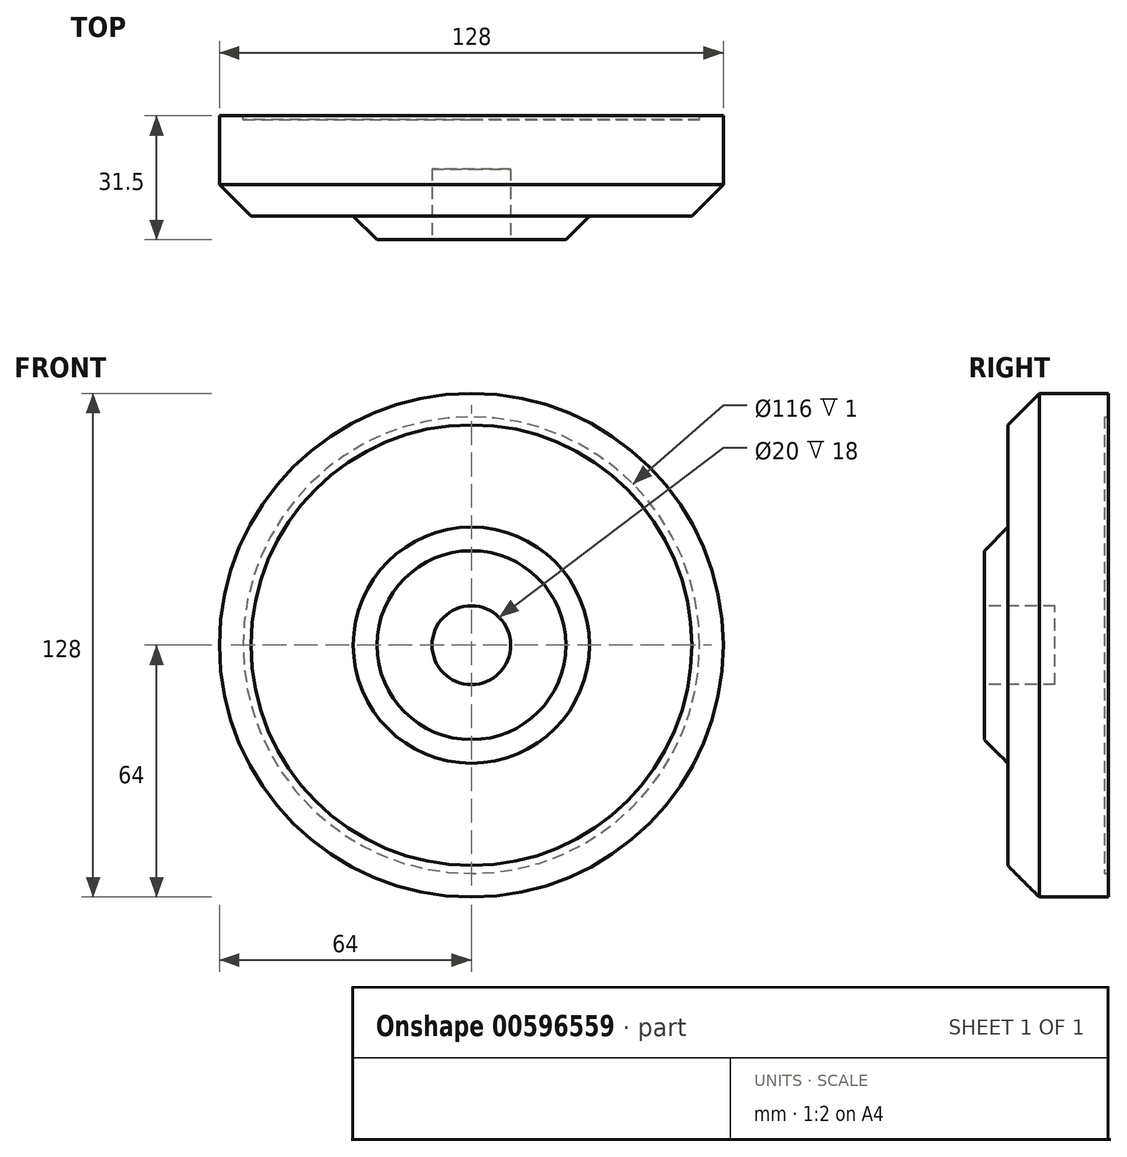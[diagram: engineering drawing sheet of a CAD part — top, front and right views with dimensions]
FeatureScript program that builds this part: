
annotation { "Feature Type Name" : "Feature", "Feature Type Description" : "" }
export const myFeature = defineFeature(function(context is Context, id is Id, definition is map)
    precondition{}
    {
        {
            var Q0;
            Q0=qCreatedBy(makeId("Front.planeOp"),FACE);
            var sketch = newSketch(context, id + "F0", { "sketchPlane" : qUnion([Q0])});
            skCircle(sketch, "E0", {"center": v(0, 0) * mm, "radius": 64 * mm});
            skSolve(sketch);
        }
        {
            var Q0;
            Q0 = qSketchRegion(id + "F0", true);
            extrude(context, id + "F1", {"entities" : qUnion([Q0]), "depth" : 25.5 * mm, "offsetDistance" : 25 * mm});
        }
        {
            var Q0;
            Q0=makeQuery(id+"F1.opExtrude","CAP_FACE",FACE,{"disambiguationData":[OSD([sQuery(id+"F0.wireOp",EDGE,"E0")])],"isStart":true});
            var sketch = newSketch(context, id + "F2", { "sketchPlane" : qUnion([Q0])});
            skCircle(sketch, "E1", {"center": v(0, 0) * mm, "radius": 58 * mm});
            skSolve(sketch);
        }
        {
            var Q0;
            Q0 = qSketchRegion(id + "F2", true);
            extrude(context, id + "F3", {"entities" : qUnion([Q0]), "operationType" : NewBodyOperationType.REMOVE, "oppositeDirection" : true, "depth" : 1 * mm, "offsetDistance" : 25 * mm});
        }
        {
            var Q0;
            Q0=makeQuery(id+"F1.opExtrude","CAP_EDGE",EDGE,{"disambiguationData":[OSD([sQuery(id+"F0.wireOp",EDGE,"E0")])],"isStart":false});
            chamfer(context, id + "F4", {"entities" : qUnion([Q0]), "width" : 8 * mm, "tangentPropagation" : true});
        }
        {
            var Q0;
            Q0=makeQuery(id+"F1.opExtrude","CAP_FACE",FACE,{"disambiguationData":[OSD([sQuery(id+"F0.wireOp",EDGE,"E0")])],"isStart":false});
            var sketch = newSketch(context, id + "F5", { "sketchPlane" : qUnion([Q0])});
            skCircle(sketch, "E2", {"center": v(0, 0) * mm, "radius": 30 * mm});
            skSolve(sketch);
        }
        {
            var Q0;
            Q0=makeQuery(id+"F5.imprint","IMPRINT",FACE,{"disambiguationData":[TD([[makeQuery(id+"F5.imprint","IMPRINT",EDGE,{"derivedFrom":sQuery(id+"F5.wireOp",EDGE,"E2")}),1.0]])]});
            extrude(context, id + "F6", {"entities" : qUnion([Q0]), "operationType" : NewBodyOperationType.ADD, "depth" : 6 * mm, "offsetDistance" : 25 * mm});
        }
        {
            var Q0;
            Q0=makeQuery(id+"F6.opExtrude","CAP_EDGE",EDGE,{"disambiguationData":[OSD([sQuery(id+"F5.wireOp",EDGE,"E2")])],"isStart":false});
            chamfer(context, id + "F7", {"entities" : qUnion([Q0]), "width" : 6 * mm, "tangentPropagation" : true});
        }
        {
            var Q0;
            Q0=makeQuery(id+"F6.opExtrude","CAP_FACE",FACE,{"disambiguationData":[OSD([sQuery(id+"F5.wireOp",EDGE,"E2")])],"isStart":false});
            var sketch = newSketch(context, id + "F8", { "sketchPlane" : qUnion([Q0])});
            skPoint(sketch, "E3", {"position": v(0, 0) * mm});
            skSolve(sketch);
        }
        {
            var Q0;
            {var subQ0=sQuery(id+"F5.wireOp",EDGE,"E2");Q0=makeQuery(id+"F8.imprint","IMPRINT",FACE,{"disambiguationData":[TD([[makeQuery(id+"F8.imprint","IMPRINT",EDGE,{"derivedFrom":makeQuery(id+"F7.opChamfer","BLEND_EDGE",EDGE,{"blendedFrom":[makeQuery(id+"F6.opExtrude","CAP_EDGE",EDGE,{"disambiguationData":[OSD([subQ0])],"isStart":false}),makeQuery(id+"F6.opExtrude","CAP_FACE",FACE,{"disambiguationData":[OSD([subQ0])],"isStart":false})],"blendedInto":[makeQuery(id+"F6.opExtrude","CAP_FACE",FACE,{"disambiguationData":[OSD([subQ0])],"isStart":false})]})}),1.0]])]});}
            var sketch = newSketch(context, id + "F9", { "sketchPlane" : qUnion([Q0])});
            skCircle(sketch, "E4", {"center": v(0, 0) * mm, "radius": 10 * mm});
            skSolve(sketch);
        }
        {
            var Q0;
            Q0 = qSketchRegion(id + "F9", true);
            extrude(context, id + "F10", {"entities" : qUnion([Q0]), "operationType" : NewBodyOperationType.REMOVE, "oppositeDirection" : true, "depth" : 18 * mm, "offsetDistance" : 25 * mm});
        }
    });
